# Revit family: QF_BPRO_RSPV 12,0_383735
name_source: partatom
category: Sonderausstattung
revit_build: Autodesk Revit 2018 (Build: 20190510_1515(x64)
units: mm (PartAtom-declared; Revit-internal decimal feet)

## family parameters
Arbeitsebenenbasiert = Nein
Beim Laden mit Abzugskörper schneiden = Nein
Bemaßung runder Anschluss = Durchmesser verwenden
Gemeinsam genutzt = Nein
Immer vertikal = Ja
Raumberechnungspunkt = Ja
Teiletyp = Normal

## types (1)
- RSPV 12,0
    Artikel Nummer = 383735
    Beschreibung = Rundriemenband zur Tablettportionierung
    Beschreibung durch Hersteller analog Leistungsverzeichniskurztext = Abmessungen

Länge: 12.000 mm
Breite: 500 mm
Höhe: 900 mm

Ausführung

Das Rundriemenband ist als selbsttragende, stabile und 
verwindungsfreie Konstruktion komplett in Chromnickel-
stahl 18/10 ausgeführt. Die Abstützung des Förderti¬sches
befindet sich ca. alle 2500 mm in Form von höhenverstell-
baren Vierkantrohrfüße 40/40 mm. Die Materialstärke des 
Bandkörpers ist 1,5 mm.
Die Bandkorpusteile sind durch Schraubstoß/Stecknaht ver-
bunden. Der Antrieb erfolgt über zwei Trommelmotoren, die
im Bandkorpus eingebaut sind. Die Umlenkrollen aus CNS 18/10
werden in einer Spannstation gehalten. Die Rundriemenführ-
ung im Unterbau ist frei zugängig und wird durch kugel-
gelagerte Kunststoffrollen geführt. Die Rundriemen haben
einen Durchmesser von 15 mm, Material PU, in hochverschleiß-
fester lebensmittelbeständiger Qualität. Der Rundriemen-
abstand zueinander ist 220 mm.
Der Sensor-Endschalter befindet sich am Bandende. Am Band-
anfang und am Bandende ist jeweils ein Not-Aus-Taster
angebracht. Der Antrieb ist stufenlos regelbar von 2,5 - 12 m/min. 
Die Steuerung ist einschließlich des Motorschutzschalters in
einem Schaltschrank aus CNS 18/10 im Unterbau eingebaut.
Die Verdrahtung wird nach VDE-Richtlinien durchgeführt. 
In Verbindung mit Steckdosen ist ein FI-Schutzschalter
obligatorisch.
Einfachste Reinigung durch Anheben der Rundriemen ist möglich.

Zubehör/ Optionen

•	Schukosteckdose 230V
•	CCE-Steckdose 230 V
•	CCE-Steckdose 400 V
•	Kabelkanal (beidseitig)
•	zusätzlicher EIN/ AUS – Taster
•	Fußschalter mit Trenntrafo (EIN/ AUS)
•	beidseitiges Stoßschutzprofil
•	Schwenktisch für Patientenkarten (max. Beladung: 5 kg)
•	Klapptisch

Technische Daten

Werkstoff:	CNS 18/10
	Rundriemen - PU
Abstützung:	alle 2500 mm
Abstand der Rundriemen:	220 mm
Durchmesser Rundriemen:	15 mm
Antriebregelung:	2,5 – 12 m/min
Elektr. Anschluß:	400 V/ 3NPE
Elektr. Anschluß Trommelmotor:	230 V/50 Hz/ 0,32 kW
Normen: Schutzart IP X5 nach DIN 40050; CE-konform; 
Steckdosen IP X4
Emissionen: Der arbeitsplatz-bezogene Schallpegel des Geräts 
ist kleiner als 70 dB(A)

Besonderheit
•	Wartungsfreier Trommelmotor

Fabrikat

Hersteller: 	B.PRO
Modell:                                 RSPV
Best.Nr.:                               383 735
    Beschreibung durch Hersteller analog Leistungsverzeichnislangtext = Abmessungen

Länge: 12.000 mm
Breite: 500 mm
Höhe: 900 mm

Ausführung

Das Rundriemenband ist als selbsttragende, stabile und 
verwindungsfreie Konstruktion komplett in Chromnickel-
stahl 18/10 ausgeführt. Die Abstützung des Förderti¬sches
befindet sich ca. alle 2500 mm in Form von höhenverstell-
baren Vierkantrohrfüße 40/40 mm. Die Materialstärke des 
Bandkörpers ist 1,5 mm.
Die Bandkorpusteile sind durch Schraubstoß/Stecknaht ver-
bunden. Der Antrieb erfolgt über zwei Trommelmotoren, die
im Bandkorpus eingebaut sind. Die Umlenkrollen aus CNS 18/10
werden in einer Spannstation gehalten. Die Rundriemenführ-
ung im Unterbau ist frei zugängig und wird durch kugel-
gelagerte Kunststoffrollen geführt. Die Rundriemen haben
einen Durchmesser von 15 mm, Material PU, in hochverschleiß-
fester lebensmittelbeständiger Qualität. Der Rundriemen-
abstand zueinander ist 220 mm.
Der Sensor-Endschalter befindet sich am Bandende. Am Band-
anfang und am Bandende ist jeweils ein Not-Aus-Taster
angebracht. Der Antrieb ist stufenlos regelbar von 2,5 - 12 m/min. 
Die Steuerung ist einschließlich des Motorschutzschalters in
einem Schaltschrank aus CNS 18/10 im Unterbau eingebaut.
Die Verdrahtung wird nach VDE-Richtlinien durchgeführt. 
In Verbindung mit Steckdosen ist ein FI-Schutzschalter
obligatorisch.
Einfachste Reinigung durch Anheben der Rundriemen ist möglich.

Zubehör/ Optionen

•	Schukosteckdose 230V
•	CCE-Steckdose 230 V
•	CCE-Steckdose 400 V
•	Kabelkanal (beidseitig)
•	zusätzlicher EIN/ AUS – Taster
•	Fußschalter mit Trenntrafo (EIN/ AUS)
•	beidseitiges Stoßschutzprofil
•	Schwenktisch für Patientenkarten (max. Beladung: 5 kg)
•	Klapptisch

Technische Daten

Werkstoff:	CNS 18/10
	Rundriemen - PU
Abstützung:	alle 2500 mm
Abstand der Rundriemen:	220 mm
Durchmesser Rundriemen:	15 mm
Antriebregelung:	2,5 – 12 m/min
Elektr. Anschluß:	400 V/ 3NPE
Elektr. Anschluß Trommelmotor:	230 V/50 Hz/ 0,32 kW
Normen: Schutzart IP X5 nach DIN 40050; CE-konform; 
Steckdosen IP X4
Emissionen: Der arbeitsplatz-bezogene Schallpegel des Geräts 
ist kleiner als 70 dB(A)

Besonderheit
•	Wartungsfreier Trommelmotor

Fabrikat

Hersteller: 	B.PRO
Modell:                                 RSPV
Best.Nr.:                               383 735
    CE Kennzeichnung = Ja
    Elektrische leistung = 320 W
    Frequenz = 50 Hz
    Gerätegewicht Netto = 0.00 kg
    Großküchengerätezuordnung = Ja
    Hauptschalter integriert = Ja
    Hersteller = B.PRO GmbH
    Höhe = 900 mm  [stored 2.95276 ft]
    Internetadresse Gerätehersteller = https://www.bpro-solutions.com
    Internetadresse für Ersatzteilliste = https://www.bpro-solutions.com
    Kosten = 0 $
    Länge Gerätebreite = 12000 mm  [stored 39.3701 ft]
    Material = QF_Metal-Stainless-Steel_general
    Modell = RSPV 12,0
    Schalldruckpegel = ca. 36 dB(A)
    Spannung = 400 V
    Tiefe = 500 mm  [stored 1.64042 ft]
    Typenkommentare = Portionier-Rundriemenband 12 m lang
    URL = https://www.bpro-solutions.com
    Zubehör = Ja
    Zuleitung zum Gerät im Lieferumfang = Ja

note: [stored X ft] marks values corroborated as IEEE doubles in the binary element streams (Revit-internal decimal feet)
